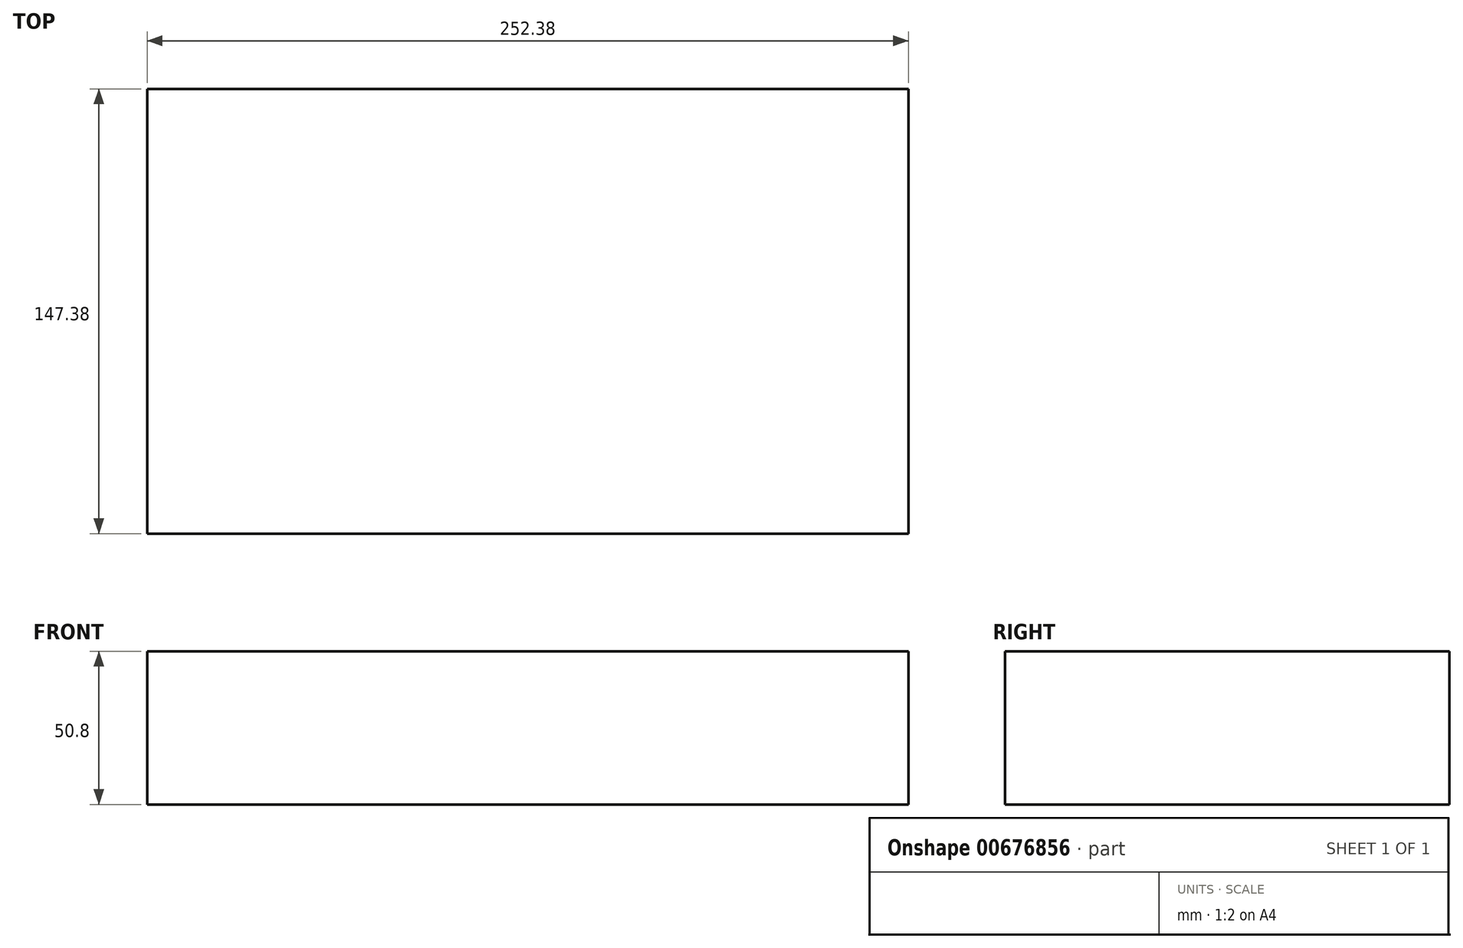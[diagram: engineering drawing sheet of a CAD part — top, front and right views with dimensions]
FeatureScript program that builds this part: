
annotation { "Feature Type Name" : "Feature", "Feature Type Description" : "" }
export const myFeature = defineFeature(function(context is Context, id is Id, definition is map)
    precondition{}
    {
        {
            var Q0;
            Q0=qCreatedBy(makeId("Top.planeOp"),FACE);
            var sketch = newSketch(context, id + "F0", { "sketchPlane" : qUnion([Q0])});
            skLineSegment(sketch, "E0.bottom", {"start": v(126.19, -73.7) * mm, "end": v(-126.19, -73.7) * mm});
            skLineSegment(sketch, "E0.top", {"start": v(126.19, 73.7) * mm, "end": v(-126.19, 73.7) * mm});
            skLineSegment(sketch, "E0.left", {"start": v(126.19, -73.7) * mm, "end": v(126.19, 73.7) * mm});
            skLineSegment(sketch, "E0.right", {"start": v(-126.19, -73.7) * mm, "end": v(-126.19, 73.7) * mm});
            skPoint(sketch, "E0.middle", {"position": v(0, 0) * mm});
            skSolve(sketch);
        }
        {
            var Q0;
            Q0=makeQuery(id+"F0.imprint","IMPRINT",FACE,{"disambiguationData":[TD([[makeQuery(id+"F0.imprint","IMPRINT",EDGE,{"derivedFrom":sQuery(id+"F0.wireOp",EDGE,"E0.bottom")}),-1.0]])]});
            extrude(context, id + "F1", {"entities" : qUnion([Q0]), "oppositeDirection" : true, "depth" : 50.8 * mm, "offsetDistance" : 25.4 * mm});
        }
    });
